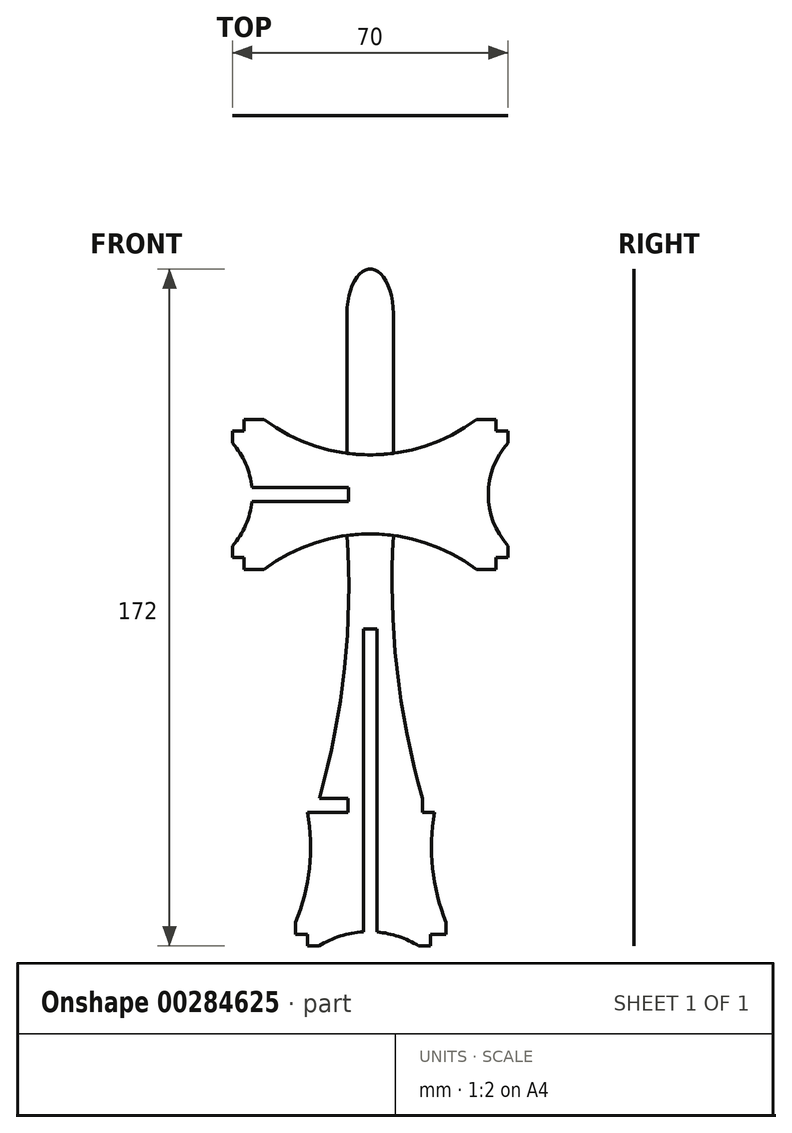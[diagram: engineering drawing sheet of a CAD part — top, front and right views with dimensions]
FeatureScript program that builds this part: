
annotation { "Feature Type Name" : "Feature", "Feature Type Description" : "" }
export const myFeature = defineFeature(function(context is Context, id is Id, definition is map)
    precondition{}
    {
        {
            var Q0;
            Q0=qCreatedBy(makeId("Front.planeOp"),FACE);
            var sketch = newSketch(context, id + "F0", { "sketchPlane" : qUnion([Q0])});
            skLineSegment(sketch, "E0.bottom", {"start": v(35, -19.05) * mm, "end": v(-35, -19.05) * mm});
            skLineSegment(sketch, "E0.top", {"start": v(35, 19.05) * mm, "end": v(-35, 19.05) * mm});
            skLineSegment(sketch, "E0.left", {"start": v(35, -19.05) * mm, "end": v(35, 19.05) * mm});
            skLineSegment(sketch, "E0.right", {"start": v(-35, -19.05) * mm, "end": v(-35, 19.05) * mm});
            skPoint(sketch, "E0.middle", {"position": v(0, 0) * mm});
            skLineSegment(sketch, "E1", {"start": v(-32, 19.05) * mm, "end": v(-32, -19.05) * mm});
            skLineSegment(sketch, "E2", {"start": v(32, 19.05) * mm, "end": v(32, -19.05) * mm});
            skLineSegment(sketch, "E3", {"start": v(-32, 16.05) * mm, "end": v(-35, 16.05) * mm});
            skLineSegment(sketch, "E4", {"start": v(32, 16.05) * mm, "end": v(35, 16.05) * mm});
            skLineSegment(sketch, "E5", {"start": v(-32, -16.05) * mm, "end": v(-35, -16.05) * mm});
            skLineSegment(sketch, "E6", {"start": v(32, -16.05) * mm, "end": v(35, -16.05) * mm});
            skArc(sketch, "E7", {"start": v(-35, -13.05) * mm, "mid": v(-30, 0) * mm, "end": v(-35, 13.05) * mm});
            skArc(sketch, "E8", {"start": v(35, 13.05) * mm, "mid": v(30, 0) * mm, "end": v(35, -13.05) * mm});
            skLineSegment(sketch, "E9", {"start": v(-30.08, 1.75) * mm, "end": v(-5.5, 1.75) * mm});
            skLineSegment(sketch, "E10", {"start": v(-5.5, 1.75) * mm, "end": v(-5.5, -1.75) * mm});
            skLineSegment(sketch, "E11", {"start": v(-5.5, -1.75) * mm, "end": v(-30.08, -1.75) * mm});
            skPoint(sketch, "E12", {"position": v(-5.5, 0) * mm});
            skLineSegment(sketch, "E13", {"start": v(-30, 0) * mm, "end": v(30, 0) * mm});
            skArc(sketch, "E14", {"start": v(-27, 19.05) * mm, "mid": v(0, 10.05) * mm, "end": v(27, 19.05) * mm});
            skArc(sketch, "E15", {"start": v(27, -19.05) * mm, "mid": v(0, -10.05) * mm, "end": v(-27, -19.05) * mm});
            skSolve(sketch);
        }
        {
            var Q0;
            {var subQ0=sQuery(id+"F0.wireOp",EDGE,"E6");Q0=makeQuery(id+"F0.imprint","IMPRINT",FACE,{"disambiguationData":[TD([[makeQuery(id+"F0.imprint","IMPRINT",EDGE,{"derivedFrom":subQ0}),1.0]])]});}
            var Q1;
            {var subQ0=sQuery(id+"F0.wireOp",EDGE,"E4");Q1=makeQuery(id+"F0.imprint","IMPRINT",FACE,{"disambiguationData":[TD([[makeQuery(id+"F0.imprint","IMPRINT",EDGE,{"derivedFrom":subQ0}),-1.0]])]});}
            var Q2;
            {var subQ0=sQuery(id+"F0.wireOp",EDGE,"E5");Q2=makeQuery(id+"F0.imprint","IMPRINT",FACE,{"disambiguationData":[TD([[makeQuery(id+"F0.imprint","IMPRINT",EDGE,{"derivedFrom":subQ0}),-1.0]])]});}
            var Q3;
            {var subQ0=sQuery(id+"F0.wireOp",EDGE,"E3");Q3=makeQuery(id+"F0.imprint","IMPRINT",FACE,{"disambiguationData":[TD([[makeQuery(id+"F0.imprint","IMPRINT",EDGE,{"derivedFrom":subQ0}),1.0]])]});}
            var Q4;
            {var subQ9=sQuery(id+"F0.wireOp",EDGE,"E11");Q4=makeQuery(id+"F0.imprint","IMPRINT",FACE,{"disambiguationData":[TD([[makeQuery(id+"F0.imprint","IMPRINT",EDGE,{"derivedFrom":subQ9}),1.0]])]});}
            var Q5;
            {var subQ1=sQuery(id+"F0.wireOp",EDGE,"E9");Q5=makeQuery(id+"F0.imprint","IMPRINT",FACE,{"disambiguationData":[TD([[makeQuery(id+"F0.imprint","IMPRINT",EDGE,{"derivedFrom":subQ1}),1.0]])]});}
            extrude(context, id + "F1", {"entities" : qUnion([Q0, Q1, Q2, Q3, Q4, Q5]), "depth" : 1 / 203.2 * mm});
        }
        {
            var Q0;
            Q0=makeQuery(id+"F1.opExtrude","CAP_FACE",FACE,{"disambiguationData":[OSD([sQuery(id+"F0.wireOp",EDGE,"E0.bottom"),sQuery(id+"F0.wireOp",EDGE,"E0.top"),sQuery(id+"F0.wireOp",EDGE,"E0.left"),sQuery(id+"F0.wireOp",EDGE,"E0.right"),sQuery(id+"F0.wireOp",EDGE,"E1"),sQuery(id+"F0.wireOp",EDGE,"E2"),sQuery(id+"F0.wireOp",EDGE,"E3"),sQuery(id+"F0.wireOp",EDGE,"E4"),sQuery(id+"F0.wireOp",EDGE,"E5"),sQuery(id+"F0.wireOp",EDGE,"E6"),sQuery(id+"F0.wireOp",EDGE,"E7"),sQuery(id+"F0.wireOp",EDGE,"E8"),sQuery(id+"F0.wireOp",EDGE,"E9"),sQuery(id+"F0.wireOp",EDGE,"E10"),sQuery(id+"F0.wireOp",EDGE,"E11"),sQuery(id+"F0.wireOp",EDGE,"E14"),sQuery(id+"F0.wireOp",EDGE,"E15")])],"isStart":false});
            var sketch = newSketch(context, id + "F2", { "sketchPlane" : qUnion([Q0])});
            skLineSegment(sketch, "E16.bottom", {"start": v(-5.9, 10.44) * mm, "end": v(5.9, 10.44) * mm});
            skLineSegment(sketch, "E16.top", {"start": v(-5.9, 45.99) * mm, "end": v(5.9, 45.99) * mm});
            skLineSegment(sketch, "E16.left", {"start": v(-5.9, 10.44) * mm, "end": v(-5.9, 45.99) * mm});
            skLineSegment(sketch, "E16.right", {"start": v(5.9, 10.44) * mm, "end": v(5.9, 45.99) * mm});
            skEllipse(sketch, "E17", {"center": v(0, 45.99) * mm, "majorRadius": 11.27 * mm, "minorRadius": 5.9 * mm, "majorAxis": v(0, -1)});
            skPoint(sketch, "E18", {"position": v(0, 10.44) * mm});
            skLineSegment(sketch, "E19.bottom", {"start": v(-5.9, -10.44) * mm, "end": v(5.9, -10.44) * mm});
            skLineSegment(sketch, "E19.top", {"start": v(-5.9, -114.74) * mm, "end": v(5.9, -114.74) * mm});
            skPoint(sketch, "E20", {"position": v(0, 57.26) * mm});
            skPoint(sketch, "E21.oppositeSnap0", {"position": v(0, -114.74) * mm});
            skLineSegment(sketch, "E21.bottom", {"start": v(-18.93, -77.27) * mm, "end": v(19.3, -77.27) * mm});
            skLineSegment(sketch, "E21.top", {"start": v(-18.93, -114.74) * mm, "end": v(19.3, -114.74) * mm});
            skLineSegment(sketch, "E21.left", {"start": v(-18.93, -77.27) * mm, "end": v(-18.93, -114.74) * mm});
            skLineSegment(sketch, "E21.right", {"start": v(19.3, -77.27) * mm, "end": v(19.3, -114.74) * mm});
            skPoint(sketch, "E22", {"position": v(0.18, -77.27) * mm});
            skLineSegment(sketch, "E23.left", {"start": v(-18.93, -77.27) * mm, "end": v(-18.93, -80.27) * mm});
            skLineSegment(sketch, "E24.bottom", {"start": v(19.3, -77.27) * mm, "end": v(16.3, -77.27) * mm});
            skLineSegment(sketch, "E24.left", {"start": v(19.3, -77.27) * mm, "end": v(19.3, -80.27) * mm});
            skLineSegment(sketch, "E25.bottom", {"start": v(-18.93, -114.74) * mm, "end": v(-16, -114.74) * mm});
            skLineSegment(sketch, "E25.top", {"start": v(-18.93, -111.74) * mm, "end": v(-16, -111.74) * mm});
            skLineSegment(sketch, "E25.left", {"start": v(-18.93, -114.74) * mm, "end": v(-18.93, -111.74) * mm});
            skLineSegment(sketch, "E25.right", {"start": v(-16, -114.74) * mm, "end": v(-16, -111.74) * mm});
            skLineSegment(sketch, "E26.bottom", {"start": v(19.3, -114.74) * mm, "end": v(15.31, -114.74) * mm});
            skLineSegment(sketch, "E26.top", {"start": v(19.3, -111.74) * mm, "end": v(15.31, -111.74) * mm});
            skLineSegment(sketch, "E26.left", {"start": v(19.3, -114.74) * mm, "end": v(19.3, -111.74) * mm});
            skLineSegment(sketch, "E26.right", {"start": v(15.31, -114.74) * mm, "end": v(15.31, -111.74) * mm});
            skLineSegment(sketch, "E27.bottom", {"start": v(-15.93, -77.27) * mm, "end": v(-12.93, -77.27) * mm});
            skLineSegment(sketch, "E27.top", {"start": v(-15.93, -80.77) * mm, "end": v(-12.93, -80.77) * mm});
            skLineSegment(sketch, "E27.left", {"start": v(-15.93, -77.27) * mm, "end": v(-15.93, -80.77) * mm});
            skLineSegment(sketch, "E27.right", {"start": v(-12.93, -77.27) * mm, "end": v(-12.93, -80.77) * mm});
            skLineSegment(sketch, "E28.bottom", {"start": v(16.3, -77.27) * mm, "end": v(13.3, -77.27) * mm});
            skLineSegment(sketch, "E28.top", {"start": v(16.3, -80.77) * mm, "end": v(13.3, -80.77) * mm});
            skLineSegment(sketch, "E28.left", {"start": v(16.3, -77.27) * mm, "end": v(16.3, -80.77) * mm});
            skLineSegment(sketch, "E28.right", {"start": v(13.3, -77.27) * mm, "end": v(13.3, -80.77) * mm});
            skArc(sketch, "E29", {"start": v(-18.93, -108.74) * mm, "mid": v(-15.47, -94.96) * mm, "end": v(-15.93, -80.77) * mm});
            skArc(sketch, "E30", {"start": v(16.3, -80.77) * mm, "mid": v(15.81, -94.97) * mm, "end": v(19.3, -108.74) * mm});
            skArc(sketch, "E31", {"start": v(12.31, -114.74) * mm, "mid": v(-0.34, -111.1) * mm, "end": v(-13, -114.74) * mm});
            skArc(sketch, "E32", {"start": v(-12.93, -77.27) * mm, "mid": v(-6.52, -44.16) * mm, "end": v(-5.9, -10.44) * mm});
            skArc(sketch, "E33", {"start": v(5.9, -10.44) * mm, "mid": v(6.75, -44.17) * mm, "end": v(13.3, -77.27) * mm});
            skSolve(sketch);
        }
        {
            var Q0;
            {var subQ0=sQuery(id+"F2.wireOp",EDGE,"E16.top");Q0=makeQuery(id+"F2.imprint","IMPRINT",FACE,{"disambiguationData":[TD([[makeQuery(id+"F2.imprint","IMPRINT",EDGE,{"derivedFrom":subQ0}),1.0]])]});}
            var Q1;
            Q1=makeQuery(id+"F2.imprint","IMPRINT",FACE,{"disambiguationData":[TD([[makeQuery(id+"F2.imprint","IMPRINT",EDGE,{"derivedFrom":sQuery(id+"F2.wireOp",EDGE,"E16.bottom")}),1.0]])]});
            var Q2;
            {var subQ0=sQuery(id+"F2.wireOp",EDGE,"E16.top");Q2=makeQuery(id+"F2.imprint","IMPRINT",FACE,{"disambiguationData":[TD([[makeQuery(id+"F2.imprint","IMPRINT",EDGE,{"derivedFrom":subQ0}),-1.0]])]});}
            var Q3;
            Q3=makeQuery(id+"F2.imprint","IMPRINT",FACE,{"disambiguationData":[TD([[makeQuery(id+"F2.imprint","IMPRINT",EDGE,{"derivedFrom":sQuery(id+"F2.wireOp",EDGE,"E19.bottom")}),-1.0]])]});
            var Q4;
            {var subQ7=sQuery(id+"F2.wireOp",EDGE,"E25.top");Q4=makeQuery(id+"F2.imprint","IMPRINT",FACE,{"disambiguationData":[TD([[makeQuery(id+"F2.imprint","IMPRINT",EDGE,{"derivedFrom":subQ7}),1.0]])]});}
            var Q5;
            {var subQ0=sQuery(id+"F2.wireOp",EDGE,"E16.bottom");Q5=makeQuery(id+"F2.imprint","IMPRINT",FACE,{"disambiguationData":[TD([[makeQuery(id+"F2.imprint","IMPRINT",EDGE,{"derivedFrom":subQ0}),-1.0]])]});}
            var Q6;
            {var subQ0=sQuery(id+"F2.wireOp",EDGE,"E19.bottom");Q6=makeQuery(id+"F2.imprint","IMPRINT",FACE,{"disambiguationData":[TD([[makeQuery(id+"F2.imprint","IMPRINT",EDGE,{"derivedFrom":subQ0}),1.0]])]});}
            extrude(context, id + "F3", {"entities" : qUnion([Q0, Q1, Q2, Q3, Q4, Q5, Q6]), "oppositeDirection" : true, "depth" : 1 / 203.2 * mm});
        }
        {
            var Q0;
            Q0=makeQuery(id+"F3.opExtrude","CAP_FACE",FACE,{"disambiguationData":[OSD([sQuery(id+"F0.wireOp",EDGE,"E15"),sQuery(id+"F2.wireOp",EDGE,"E21.top"),sQuery(id+"F2.wireOp",EDGE,"E21.left"),sQuery(id+"F2.wireOp",EDGE,"E21.right"),sQuery(id+"F2.wireOp",EDGE,"E25.top"),sQuery(id+"F2.wireOp",EDGE,"E25.right"),sQuery(id+"F2.wireOp",EDGE,"E26.top"),sQuery(id+"F2.wireOp",EDGE,"E26.right"),sQuery(id+"F2.wireOp",EDGE,"E27.top"),sQuery(id+"F2.wireOp",EDGE,"E27.right"),sQuery(id+"F2.wireOp",EDGE,"E28.top"),sQuery(id+"F2.wireOp",EDGE,"E28.right"),sQuery(id+"F2.wireOp",EDGE,"E29"),sQuery(id+"F2.wireOp",EDGE,"E30"),sQuery(id+"F2.wireOp",EDGE,"E31"),sQuery(id+"F2.wireOp",EDGE,"E32"),sQuery(id+"F2.wireOp",EDGE,"E33")])],"isStart":true});
            var sketch = newSketch(context, id + "F4", { "sketchPlane" : qUnion([Q0])});
            skLineSegment(sketch, "E34", {"start": v(-1.75, -111.14) * mm, "end": v(-1.75, -34.19) * mm});
            skLineSegment(sketch, "E35", {"start": v(-1.75, -34.19) * mm, "end": v(1.75, -34.19) * mm});
            skLineSegment(sketch, "E36", {"start": v(1.75, -34.19) * mm, "end": v(1.75, -111.19) * mm});
            skPoint(sketch, "E37", {"position": v(0, -34.19) * mm});
            skLineSegment(sketch, "E38", {"start": v(-12.93, -77.27) * mm, "end": v(-5.66, -77.27) * mm});
            skLineSegment(sketch, "E39", {"start": v(-5.66, -77.27) * mm, "end": v(-5.66, -80.77) * mm});
            skLineSegment(sketch, "E40", {"start": v(-5.66, -80.77) * mm, "end": v(-12.93, -80.77) * mm});
            skSolve(sketch);
        }
        {
            var Q0;
            Q0 = qSketchRegion(id + "F4", true);
            var Q1;
            {var subQ0=sQuery(id+"F4.wireOp",EDGE,"E34");Q1=makeQuery(id+"F4.imprint","IMPRINT",FACE,{"disambiguationData":[TD([[makeQuery(id+"F4.imprint","IMPRINT",EDGE,{"derivedFrom":subQ0}),-1.0]])]});}
            var Q2;
            Q2=makeQuery(id+"F4.imprint","IMPRINT",FACE,{"disambiguationData":[TD([[makeQuery(id+"F4.imprint","IMPRINT",EDGE,{"derivedFrom":sQuery(id+"F4.wireOp",EDGE,"E38")}),-1.0]])]});
            extrude(context, id + "F5", {"entities" : qUnion([Q0, Q1, Q2]), "operationType" : NewBodyOperationType.REMOVE, "endBound" : BoundingType.THROUGH_ALL, "oppositeDirection" : true, "depth" : 25 * mm});
        }
    });
